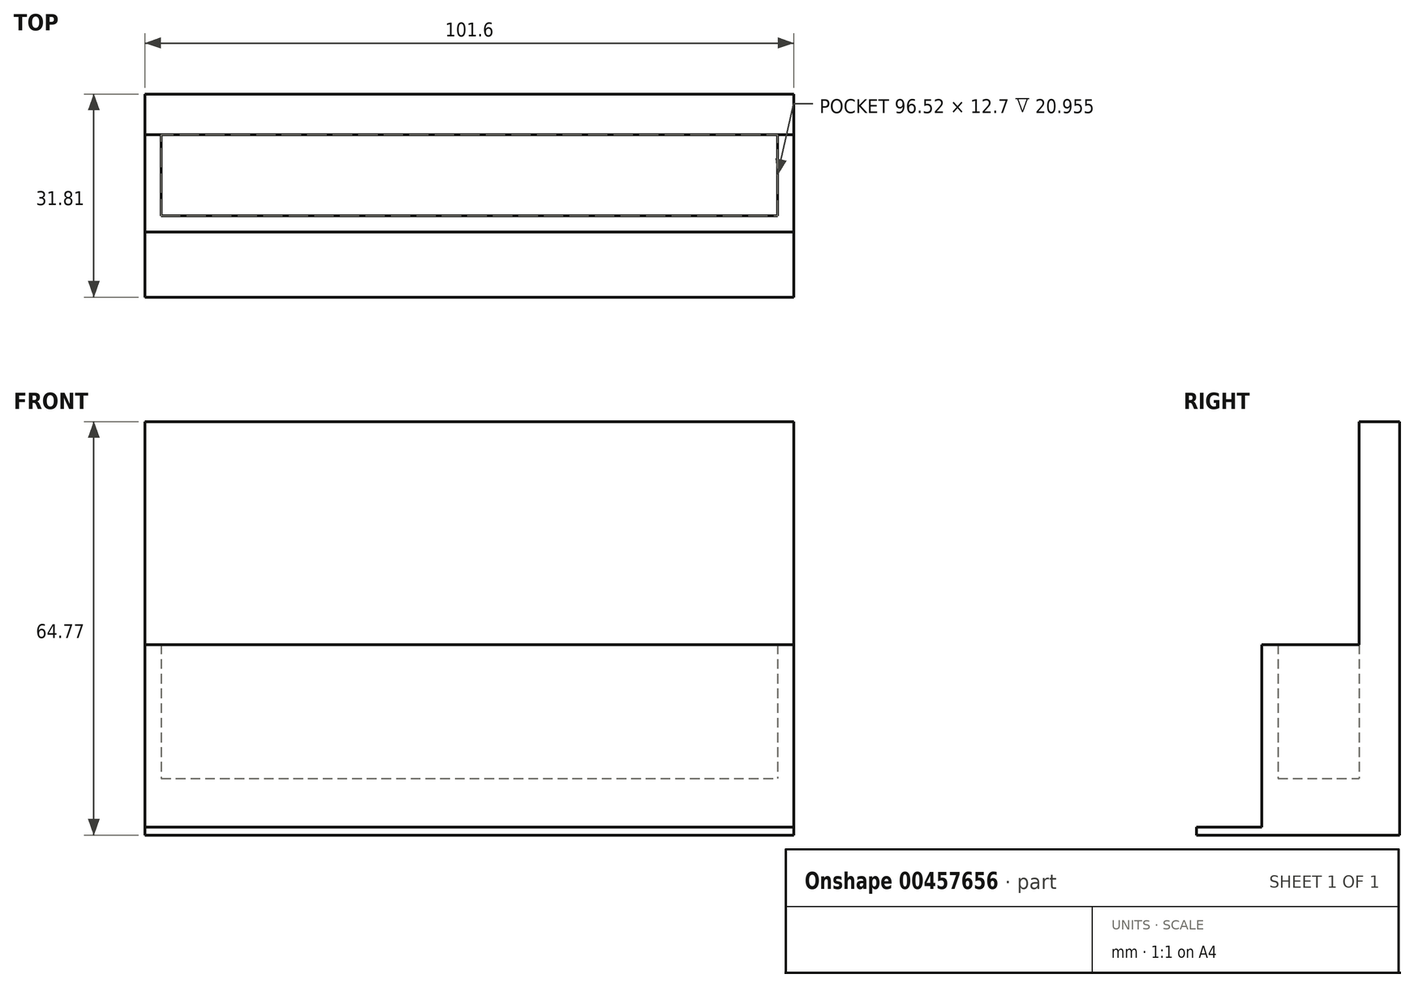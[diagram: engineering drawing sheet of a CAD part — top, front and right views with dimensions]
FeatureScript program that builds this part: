
annotation { "Feature Type Name" : "Feature", "Feature Type Description" : "" }
export const myFeature = defineFeature(function(context is Context, id is Id, definition is map)
    precondition{}
    {
        {
            var Q0;
            Q0=qCreatedBy(makeId("Front.planeOp"),FACE);
            var sketch = newSketch(context, id + "F0", { "sketchPlane" : qUnion([Q0])});
            skLineSegment(sketch, "E0.bottom", {"start": v(-71.86, -13.66) * mm, "end": v(29.74, -13.66) * mm});
            skLineSegment(sketch, "E0.top", {"start": v(-71.86, -77.16) * mm, "end": v(29.74, -77.16) * mm});
            skLineSegment(sketch, "E0.left", {"start": v(-71.86, -13.66) * mm, "end": v(-71.86, -77.16) * mm});
            skLineSegment(sketch, "E0.right", {"start": v(29.74, -13.66) * mm, "end": v(29.74, -77.16) * mm});
            skSolve(sketch);
        }
        {
            var Q0;
            Q0=makeQuery(id+"F0.imprint","IMPRINT",FACE,{"disambiguationData":[TD([[makeQuery(id+"F0.imprint","IMPRINT",EDGE,{"derivedFrom":sQuery(id+"F0.wireOp",EDGE,"E0.bottom")}),-1.0]])]});
            extrude(context, id + "F1", {"entities" : qUnion([Q0]), "depth" : 6.35 * mm});
        }
        {
            var Q0;
            Q0=makeQuery(id+"F1.opExtrude","CAP_FACE",FACE,{"disambiguationData":[OSD([sQuery(id+"F0.wireOp",EDGE,"E0.bottom"),sQuery(id+"F0.wireOp",EDGE,"E0.top"),sQuery(id+"F0.wireOp",EDGE,"E0.left"),sQuery(id+"F0.wireOp",EDGE,"E0.right")])],"isStart":false});
            var sketch = newSketch(context, id + "F2", { "sketchPlane" : qUnion([Q0])});
            skLineSegment(sketch, "E1.bottom", {"start": v(-71.86, -77.16) * mm, "end": v(29.74, -77.16) * mm});
            skLineSegment(sketch, "E1.top", {"start": v(-71.86, -69.54) * mm, "end": v(29.74, -69.54) * mm});
            skLineSegment(sketch, "E1.left", {"start": v(-71.86, -77.16) * mm, "end": v(-71.86, -69.54) * mm});
            skLineSegment(sketch, "E1.right", {"start": v(29.74, -77.16) * mm, "end": v(29.74, -69.54) * mm});
            skSolve(sketch);
        }
        {
            var Q0;
            Q0=makeQuery(id+"F2.imprint","IMPRINT",FACE,{"disambiguationData":[TD([[makeQuery(id+"F2.imprint","IMPRINT",EDGE,{"derivedFrom":sQuery(id+"F2.wireOp",EDGE,"E1.bottom")}),1.0]])]});
            extrude(context, id + "F3", {"entities" : qUnion([Q0]), "operationType" : NewBodyOperationType.ADD, "depth" : 15.24 * mm});
        }
        {
            var Q0;
            Q0=makeQuery(id+"F3.opExtrude","SWEPT_FACE",FACE,{"disambiguationData":[OSD([sQuery(id+"F2.wireOp",EDGE,"E1.top")])]});
            var sketch = newSketch(context, id + "F4", { "sketchPlane" : qUnion([Q0])});
            skLineSegment(sketch, "E2.bottom", {"start": v(-71.86, -21.59) * mm, "end": v(29.74, -21.59) * mm});
            skLineSegment(sketch, "E2.top", {"start": v(-69.32, -19.05) * mm, "end": v(27.2, -19.05) * mm});
            skLineSegment(sketch, "E2.left", {"start": v(-71.86, -21.59) * mm, "end": v(-71.86, -19.05) * mm});
            skLineSegment(sketch, "E2.right", {"start": v(29.74, -21.59) * mm, "end": v(29.74, -19.05) * mm});
            skLineSegment(sketch, "E3.bottom", {"start": v(-71.86, -21.59) * mm, "end": v(-69.32, -21.59) * mm});
            skLineSegment(sketch, "E3.top", {"start": v(-71.86, -6.35) * mm, "end": v(-69.32, -6.35) * mm});
            skLineSegment(sketch, "E3.left", {"start": v(-71.86, -21.59) * mm, "end": v(-71.86, -6.35) * mm});
            skLineSegment(sketch, "E3.right", {"start": v(-69.32, -19.05) * mm, "end": v(-69.32, -6.35) * mm});
            skLineSegment(sketch, "E4.bottom", {"start": v(29.74, -21.59) * mm, "end": v(27.2, -21.59) * mm});
            skLineSegment(sketch, "E4.top", {"start": v(29.74, -6.35) * mm, "end": v(27.2, -6.35) * mm});
            skLineSegment(sketch, "E4.left", {"start": v(29.74, -21.59) * mm, "end": v(29.74, -6.35) * mm});
            skLineSegment(sketch, "E4.right", {"start": v(27.2, -19.05) * mm, "end": v(27.2, -6.35) * mm});
            skSolve(sketch);
        }
        {
            var Q0;
            Q0=makeQuery(id+"F4.imprint","IMPRINT",FACE,{"disambiguationData":[TD([[makeQuery(id+"F4.imprint","IMPRINT",EDGE,{"derivedFrom":sQuery(id+"F4.wireOp",EDGE,"E2.bottom")}),1.0]])]});
            extrude(context, id + "F5", {"entities" : qUnion([Q0]), "operationType" : NewBodyOperationType.ADD, "depth" : 20.95 * mm});
        }
        {
            var Q0;
            Q0=makeQuery(id+"F3.boolean.opBoolean","MERGE",FACE,{"derivedFrom":[makeQuery(id+"F1.opExtrude","SWEPT_FACE",FACE,{"disambiguationData":[OSD([sQuery(id+"F0.wireOp",EDGE,"E0.top")])]}),makeQuery(id+"F3.opExtrude","SWEPT_FACE",FACE,{"disambiguationData":[OSD([sQuery(id+"F2.wireOp",EDGE,"E1.bottom")])]})]});
            var sketch = newSketch(context, id + "F6", { "sketchPlane" : qUnion([Q0])});
            skPoint(sketch, "E5.middle", {"position": v(-21.06, 10.8) * mm});
            skPoint(sketch, "E5.middle.positionSnap0", {"position": v(-21.06, 21.59) * mm});
            skPoint(sketch, "E5.middle.positionSnap1", {"position": v(-71.86, 10.8) * mm});
            skPoint(sketch, "E5.centerSnap0", {"position": v(-21.06, 21.59) * mm});
            skPoint(sketch, "E5.centerSnap1", {"position": v(-71.86, 10.8) * mm});
            skLineSegment(sketch, "E6.bottom", {"start": v(-71.86, 0) * mm, "end": v(29.74, 0) * mm});
            skLineSegment(sketch, "E6.top", {"start": v(-71.86, 31.8) * mm, "end": v(29.74, 31.8) * mm});
            skLineSegment(sketch, "E6.left", {"start": v(-71.86, 0) * mm, "end": v(-71.86, 31.8) * mm});
            skLineSegment(sketch, "E6.right", {"start": v(29.74, 0) * mm, "end": v(29.74, 31.8) * mm});
            skSolve(sketch);
        }
        {
            var Q0;
            Q0 = qSketchRegion(id + "F6", true);
            extrude(context, id + "F7", {"entities" : qUnion([Q0]), "operationType" : NewBodyOperationType.ADD, "depth" : 1.27 * mm});
        }
        {
            var Q0;
            Q0 = qSketchRegion(id + "F6", true);
            extrude(context, id + "F8", {"entities" : qUnion([Q0]), "operationType" : NewBodyOperationType.ADD, "depth" : 1.27 * mm});
        }
    });
